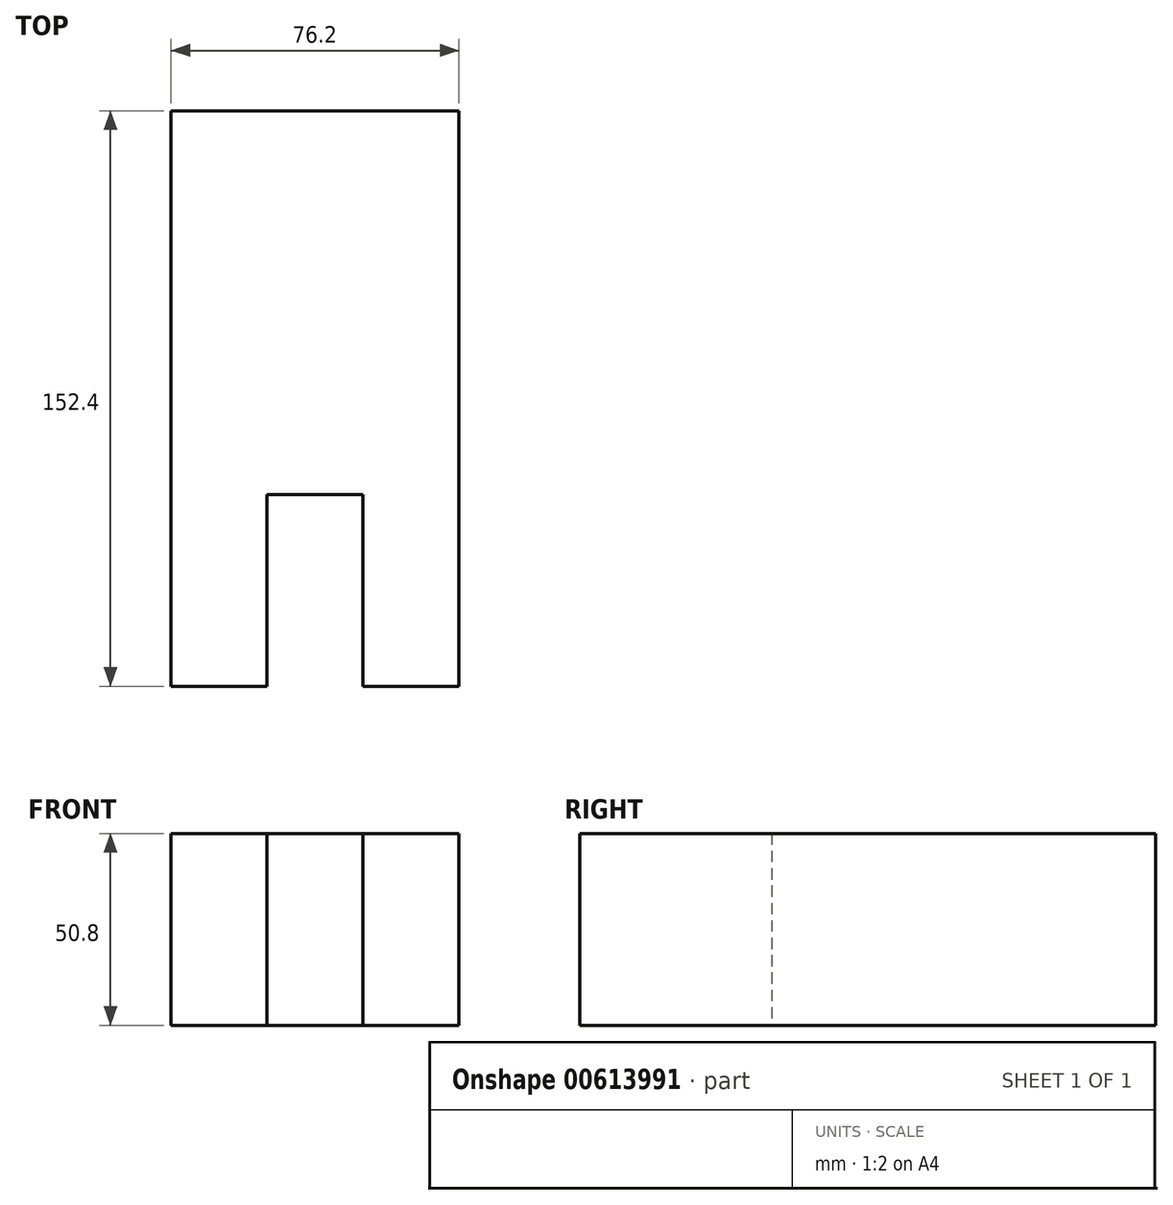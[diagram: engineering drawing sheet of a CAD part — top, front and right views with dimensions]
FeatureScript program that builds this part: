
annotation { "Feature Type Name" : "Feature", "Feature Type Description" : "" }
export const myFeature = defineFeature(function(context is Context, id is Id, definition is map)
    precondition{}
    {
        {
            var Q0;
            Q0=qCreatedBy(makeId("Top.planeOp"),FACE);
            var sketch = newSketch(context, id + "F0", { "sketchPlane" : qUnion([Q0])});
            skLineSegment(sketch, "E0", {"start": v(0, 0) * mm, "end": v(0, 152.4) * mm});
            skLineSegment(sketch, "E1", {"start": v(0, 152.4) * mm, "end": v(76.2, 152.4) * mm});
            skLineSegment(sketch, "E2", {"start": v(76.2, 152.4) * mm, "end": v(76.2, 0) * mm});
            skLineSegment(sketch, "E3", {"start": v(76.2, 0) * mm, "end": v(50.8, 0) * mm});
            skLineSegment(sketch, "E4", {"start": v(50.8, 0) * mm, "end": v(50.8, 50.8) * mm});
            skLineSegment(sketch, "E5", {"start": v(50.8, 50.8) * mm, "end": v(25.4, 50.8) * mm});
            skLineSegment(sketch, "E6", {"start": v(25.4, 50.8) * mm, "end": v(25.4, 0) * mm});
            skLineSegment(sketch, "E7", {"start": v(25.4, 0) * mm, "end": v(0, 0) * mm});
            skSolve(sketch);
        }
        {
            var Q0;
            Q0=makeQuery(id+"F0.imprint","IMPRINT",FACE,{"disambiguationData":[TD([[makeQuery(id+"F0.imprint","IMPRINT",EDGE,{"derivedFrom":sQuery(id+"F0.wireOp",EDGE,"E0")}),-1.0]])]});
            extrude(context, id + "F1", {"entities" : qUnion([Q0]), "depth" : 50.8 * mm, "offsetDistance" : 25.4 * mm});
        }
    });
